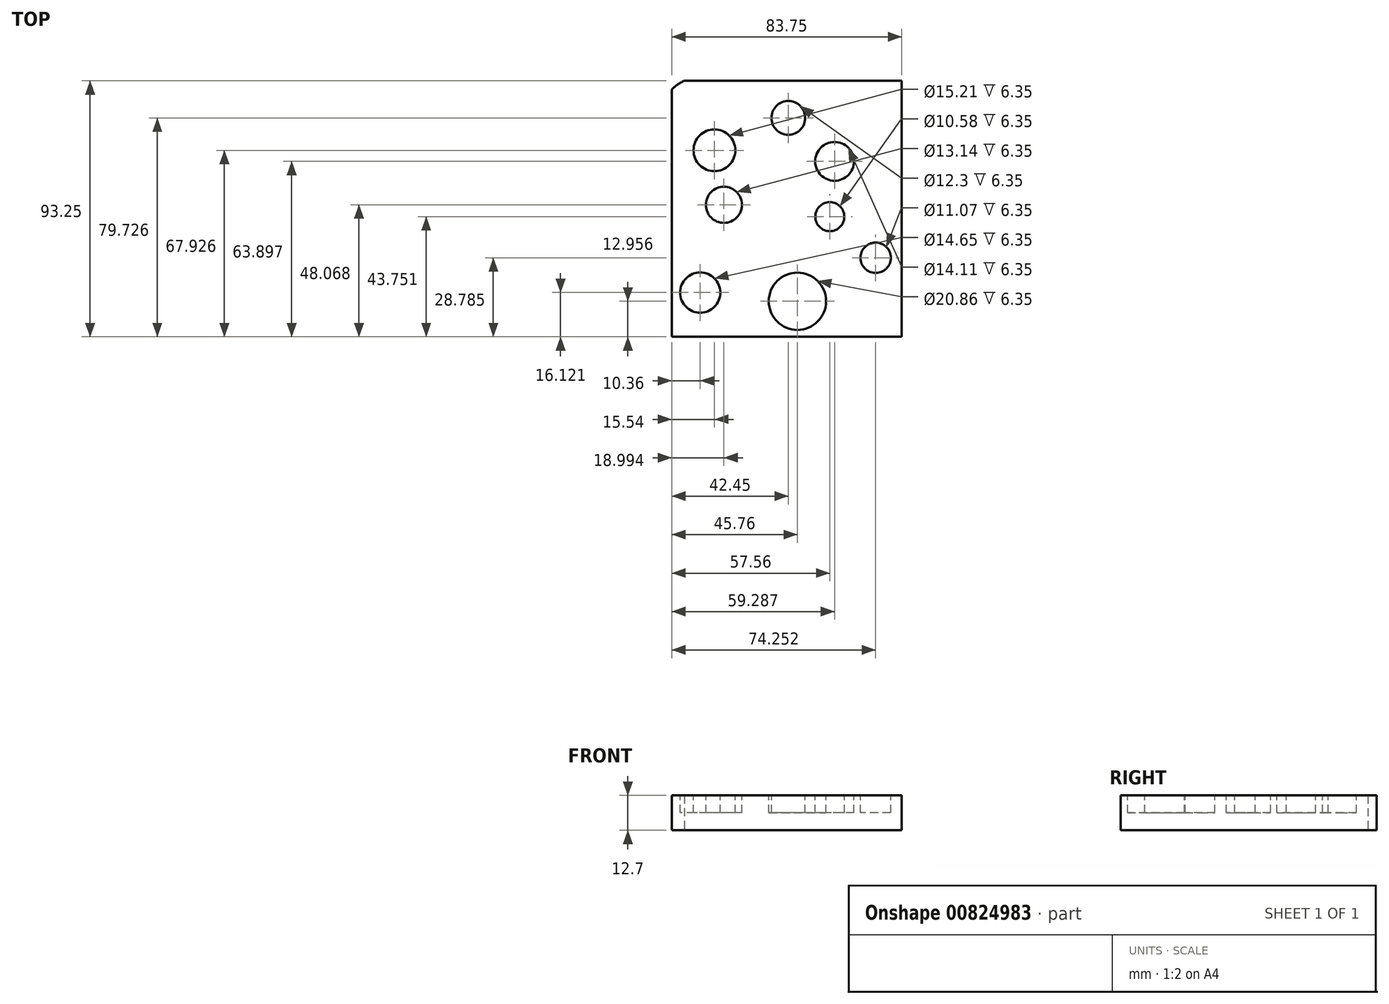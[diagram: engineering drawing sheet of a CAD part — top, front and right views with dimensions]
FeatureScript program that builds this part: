
annotation { "Feature Type Name" : "Feature", "Feature Type Description" : "" }
export const myFeature = defineFeature(function(context is Context, id is Id, definition is map)
    precondition{}
    {
        {
            var Q0;
            Q0=qCreatedBy(makeId("Top.planeOp"),FACE);
            var sketch = newSketch(context, id + "F0", { "sketchPlane" : qUnion([Q0])});
            skLineSegment(sketch, "E0.bottom", {"start": v(-42.45, 39.57) * mm, "end": v(41.3, 39.57) * mm});
            skLineSegment(sketch, "E0.top", {"start": v(-42.45, -53.68) * mm, "end": v(41.3, -53.68) * mm});
            skLineSegment(sketch, "E0.left", {"start": v(-42.45, 39.57) * mm, "end": v(-42.45, -53.68) * mm});
            skLineSegment(sketch, "E0.right", {"start": v(41.3, 39.57) * mm, "end": v(41.3, -53.68) * mm});
            skCircle(sketch, "E1", {"center": v(-28.06, -5.61) * mm, "radius": 10.32 * mm});
            skArc(sketch, "E2", {"start": v(12.5, 39.57) * mm, "mid": v(22.02, 5.27) * mm, "end": v(31.53, 39.57) * mm});
            skArc(sketch, "E3", {"start": v(-42.45, 15.1) * mm, "mid": v(-19.35, 17.29) * mm, "end": v(-25.8, 39.57) * mm});
            skArc(sketch, "E4", {"start": v(41.3, -18.61) * mm, "mid": v(32.66, -31.23) * mm, "end": v(41.3, -43.84) * mm});
            skArc(sketch, "E5", {"start": v(-4.75, -53.68) * mm, "mid": v(-15.4, -31.8) * mm, "end": v(-26.05, -53.68) * mm});
            skCircle(sketch, "E6", {"center": v(16.55, -44.47) * mm, "radius": 9.2 * mm});
            skCircle(sketch, "E7", {"center": v(20.87, -13.38) * mm, "radius": 9.23 * mm});
            skArc(sketch, "E8.trimOffspring", {"start": v(-37.8, 39.57) * mm, "mid": v(-40.27, 38.2) * mm, "end": v(-42.45, 36.4) * mm});
            skSolve(sketch);
        }
        {
            var Q0;
            Q0=makeQuery(id+"F0.imprint","IMPRINT",FACE,{"disambiguationData":[TD([[makeQuery(id+"F0.imprint","IMPRINT",EDGE,{"derivedFrom":sQuery(id+"F0.wireOp",EDGE,"E1")}),-1.0]])]});
            var Q1;
            {var subQ0=sQuery(id+"F0.wireOp",EDGE,"E2");Q1=makeQuery(id+"F0.imprint","IMPRINT",FACE,{"disambiguationData":[TD([[makeQuery(id+"F0.imprint","IMPRINT",EDGE,{"derivedFrom":subQ0}),1.0]])]});}
            var Q2;
            {var subQ0=sQuery(id+"F0.wireOp",EDGE,"E3");Q2=makeQuery(id+"F0.imprint","IMPRINT",FACE,{"disambiguationData":[TD([[makeQuery(id+"F0.imprint","IMPRINT",EDGE,{"derivedFrom":subQ0}),1.0]])]});}
            var Q3;
            {var subQ0=sQuery(id+"F0.wireOp",EDGE,"E5");Q3=makeQuery(id+"F0.imprint","IMPRINT",FACE,{"disambiguationData":[TD([[makeQuery(id+"F0.imprint","IMPRINT",EDGE,{"derivedFrom":subQ0}),1.0]])]});}
            var Q4;
            Q4=makeQuery(id+"F0.imprint","IMPRINT",FACE,{"disambiguationData":[TD([[makeQuery(id+"F0.imprint","IMPRINT",EDGE,{"derivedFrom":sQuery(id+"F0.wireOp",EDGE,"E1")}),1.0]])]});
            var Q5;
            Q5=makeQuery(id+"F0.imprint","IMPRINT",FACE,{"disambiguationData":[TD([[makeQuery(id+"F0.imprint","IMPRINT",EDGE,{"derivedFrom":sQuery(id+"F0.wireOp",EDGE,"E7")}),1.0]])]});
            var Q6;
            Q6=makeQuery(id+"F0.imprint","IMPRINT",FACE,{"disambiguationData":[TD([[makeQuery(id+"F0.imprint","IMPRINT",EDGE,{"derivedFrom":sQuery(id+"F0.wireOp",EDGE,"E6")}),1.0]])]});
            var Q7;
            {var subQ0=sQuery(id+"F0.wireOp",EDGE,"E4");Q7=makeQuery(id+"F0.imprint","IMPRINT",FACE,{"disambiguationData":[TD([[makeQuery(id+"F0.imprint","IMPRINT",EDGE,{"derivedFrom":subQ0}),1.0]])]});}
            extrude(context, id + "F1", {"entities" : qUnion([Q0, Q1, Q2, Q3, Q4, Q5, Q6, Q7]), "depth" : 12.7 * mm, "offsetDistance" : 25.4 * mm});
        }
        {
            var Q0;
            Q0=makeQuery(id+"F1.opExtrude","CAP_FACE",FACE,{"disambiguationData":[OSD([sQuery(id+"F0.wireOp",EDGE,"E0.bottom"),sQuery(id+"F0.wireOp",EDGE,"E0.top"),sQuery(id+"F0.wireOp",EDGE,"E0.left"),sQuery(id+"F0.wireOp",EDGE,"E0.right"),sQuery(id+"F0.wireOp",EDGE,"E8.trimOffspring")])],"isStart":false});
            var sketch = newSketch(context, id + "F2", { "sketchPlane" : qUnion([Q0])});
            skCircle(sketch, "E9", {"center": v(-26.9, 14.25) * mm, "radius": 7.6 * mm});
            skCircle(sketch, "E10", {"center": v(31.8, -24.9) * mm, "radius": 5.54 * mm});
            skCircle(sketch, "E11", {"center": v(-32.1, -37.56) * mm, "radius": 7.33 * mm});
            skCircle(sketch, "E12", {"center": v(16.84, 10.22) * mm, "radius": 7.06 * mm});
            skCircle(sketch, "E13", {"center": v(3.3, -40.72) * mm, "radius": 10.43 * mm});
            skCircle(sketch, "E14", {"center": v(0, 26.05) * mm, "radius": 6.15 * mm});
            skCircle(sketch, "E15", {"center": v(-23.46, -5.61) * mm, "radius": 6.57 * mm});
            skCircle(sketch, "E16", {"center": v(15.1, -9.93) * mm, "radius": 5.3 * mm});
            skSolve(sketch);
        }
        {
            var Q0;
            Q0 = qSketchRegion(id + "F2", true);
            extrude(context, id + "F3", {"entities" : qUnion([Q0]), "operationType" : NewBodyOperationType.REMOVE, "oppositeDirection" : true, "depth" : 6.35 * mm, "offsetDistance" : 25.4 * mm});
        }
    });
